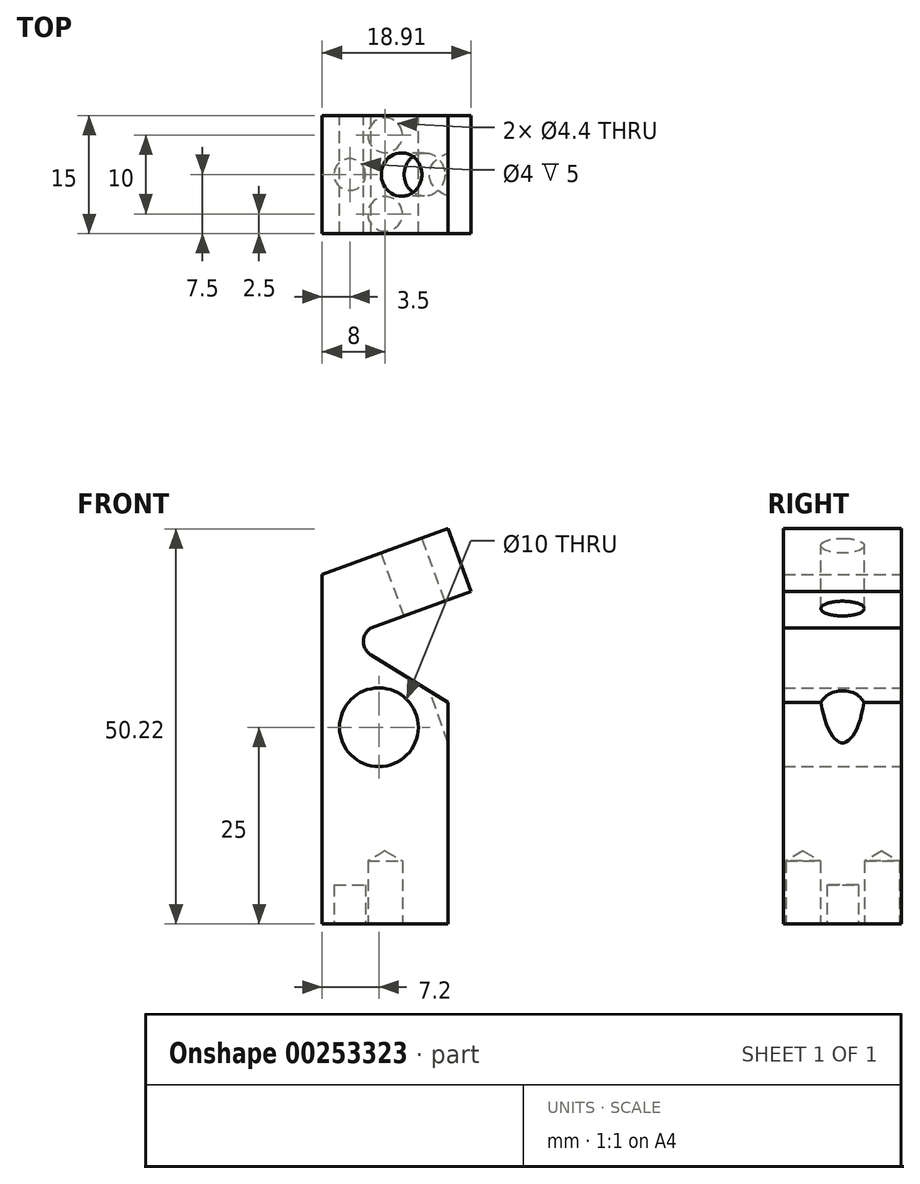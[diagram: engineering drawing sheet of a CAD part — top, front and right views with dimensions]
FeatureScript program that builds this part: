
annotation { "Feature Type Name" : "Feature", "Feature Type Description" : "" }
export const myFeature = defineFeature(function(context is Context, id is Id, definition is map)
    precondition{}
    {
        {
            var Q0;
            Q0=qCreatedBy(makeId("Front.planeOp"),FACE);
            var sketch = newSketch(context, id + "F0", { "sketchPlane" : qUnion([Q0])});
            skLineSegment(sketch, "E0", {"start": v(0, 0) * mm, "end": v(0, 44.4) * mm});
            skLineSegment(sketch, "E1", {"start": v(0, 44.4) * mm, "end": v(16, 50.22) * mm});
            skLineSegment(sketch, "E2", {"start": v(16, 50.22) * mm, "end": v(18.9, 42.24) * mm});
            skLineSegment(sketch, "E3", {"start": v(18.9, 42.24) * mm, "end": v(6.18, 37.6) * mm});
            skLineSegment(sketch, "E4", {"start": v(0, 0) * mm, "end": v(16, 0) * mm});
            skLineSegment(sketch, "E5", {"start": v(16, 0) * mm, "end": v(16, 28.18) * mm});
            skLineSegment(sketch, "E6", {"start": v(16, 28.18) * mm, "end": v(6.18, 34.2) * mm});
            skLineSegment(sketch, "E7", {"start": v(-9.9, 50.22) * mm, "end": v(46.25, 50.22) * mm, "construction": true});
            skCircle(sketch, "E8", {"center": v(7.2, 25) * mm, "radius": 5 * mm});
            skArc(sketch, "E9", {"start": v(6.18, 34.2) * mm, "mid": v(5.23, 35.9) * mm, "end": v(6.18, 37.6) * mm});
            skSolve(sketch);
        }
        {
            var Q0;
            Q0=makeQuery(id+"F0.imprint","IMPRINT",FACE,{"disambiguationData":[TD([[makeQuery(id+"F0.imprint","IMPRINT",EDGE,{"derivedFrom":sQuery(id+"F0.wireOp",EDGE,"E0")}),-1.0]])]});
            extrude(context, id + "F1", {"entities" : qUnion([Q0]), "depth" : 15 * mm});
        }
        {
            var Q0;
            Q0=makeQuery(id+"F1.opExtrude","SWEPT_FACE",FACE,{"disambiguationData":[OSD([sQuery(id+"F0.wireOp",EDGE,"E1")])]});
            var sketch = newSketch(context, id + "F2", { "sketchPlane" : qUnion([Q0])});
            skPoint(sketch, "E10", {"position": v(25.91, -7.5) * mm});
            skSolve(sketch);
        }
        {
            var Q0;
            Q0=sQuery(id+"F2.wireOp",VERTEX,"E10");
            var Q1;
            Q1=makeQuery(id+"F1.opExtrude","SWEPT_BODY",BODY,{"disambiguationData":[OSD([sQuery(id+"F0.wireOp",EDGE,"E0"),sQuery(id+"F0.wireOp",EDGE,"E1"),sQuery(id+"F0.wireOp",EDGE,"E2"),sQuery(id+"F0.wireOp",EDGE,"E3"),sQuery(id+"F0.wireOp",EDGE,"E4"),sQuery(id+"F0.wireOp",EDGE,"E5"),sQuery(id+"F0.wireOp",EDGE,"E6"),sQuery(id+"F0.wireOp",EDGE,"E8"),sQuery(id+"F0.wireOp",EDGE,"E9")])]});
            hole(context, id + "F3", {"style" : HoleStyle.SIMPLE, "endStyle" : HoleEndStyle.THROUGH, "standardTappedOrClearance" : lookupTablePath({ "standard" : "ISO", "fit" : "Normal", "size" : "M5", "type" : "Clearance" }), "standardBlindInLast" : lookupTablePath({ "fit" : "Standard", "standard" : "ISO", "size" : "M5", "type" : "Clearance" }), "holeDiameter" : 5.5 * mm, "tappedDepth" : 12 * mm, "tapClearance" : 3, "locations" : qUnion([Q0]), "scope" : qUnion([Q1])});
        }
        {
            var Q0;
            Q0=makeQuery(id+"F1.opExtrude","SWEPT_FACE",FACE,{"disambiguationData":[OSD([sQuery(id+"F0.wireOp",EDGE,"E4")])]});
            var sketch = newSketch(context, id + "F4", { "sketchPlane" : qUnion([Q0])});
            skCircle(sketch, "E11", {"center": v(3.5, 7.5) * mm, "radius": 2 * mm});
            skPoint(sketch, "E12", {"position": v(8, 12.5) * mm});
            skLineSegment(sketch, "E13", {"start": v(-11.55, 7.5) * mm, "end": v(33.8, 7.5) * mm, "construction": true});
            skPoint(sketch, "E14.MirrorP", {"position": v(8, 2.5) * mm});
            skSolve(sketch);
        }
        {
            var Q0;
            Q0=makeQuery(id+"F4.imprint","IMPRINT",FACE,{"disambiguationData":[TD([[makeQuery(id+"F4.imprint","IMPRINT",EDGE,{"derivedFrom":sQuery(id+"F4.wireOp",EDGE,"E11")}),1.0]])]});
            extrude(context, id + "F5", {"entities" : qUnion([Q0]), "operationType" : NewBodyOperationType.REMOVE, "oppositeDirection" : true, "depth" : 5 * mm});
        }
        {
            var Q0;
            Q0=sQuery(id+"F4.wireOp",VERTEX,"E12");
            var Q1;
            Q1=sQuery(id+"F4.wireOp",VERTEX,"E14.MirrorP");
            var Q2;
            Q2=makeQuery(id+"F1.opExtrude","SWEPT_BODY",BODY,{"disambiguationData":[OSD([sQuery(id+"F0.wireOp",EDGE,"E0"),sQuery(id+"F0.wireOp",EDGE,"E1"),sQuery(id+"F0.wireOp",EDGE,"E2"),sQuery(id+"F0.wireOp",EDGE,"E3"),sQuery(id+"F0.wireOp",EDGE,"E4"),sQuery(id+"F0.wireOp",EDGE,"E5"),sQuery(id+"F0.wireOp",EDGE,"E6"),sQuery(id+"F0.wireOp",EDGE,"E8"),sQuery(id+"F0.wireOp",EDGE,"E9")])]});
            hole(context, id + "F6", {"style" : HoleStyle.SIMPLE, "endStyle" : HoleEndStyle.BLIND, "standardTappedOrClearance" : lookupTablePath({ "standard" : "ISO", "fit" : "Normal", "size" : "M4", "type" : "Clearance" }), "standardBlindInLast" : lookupTablePath({ "fit" : "Standard", "standard" : "ISO", "size" : "M4", "type" : "Clearance" }), "holeDiameter" : 4.4 * mm, "holeDepth" : 8 * mm, "tappedDepth" : 12 * mm, "tapClearance" : 3, "locations" : qUnion([Q0, Q1]), "scope" : qUnion([Q2])});
        }
        {
            var Q0;
            Q0=makeQuery(id+"F1.opExtrude","SWEPT_FACE",FACE,{"disambiguationData":[OSD([sQuery(id+"F0.wireOp",EDGE,"E3")])]});
            var sketch = newSketch(context, id + "F7", { "sketchPlane" : qUnion([Q0])});
            skCircle(sketch, "E15", {"center": v(25.91, 7.5) * mm, "radius": 3 * mm});
            skSolve(sketch);
        }
        {
            var Q0;
            Q0 = qSketchRegion(id + "F7", true);
            extrude(context, id + "F8", {"entities" : qUnion([Q0]), "operationType" : NewBodyOperationType.REMOVE, "depth" : 25 * mm});
        }
    });
